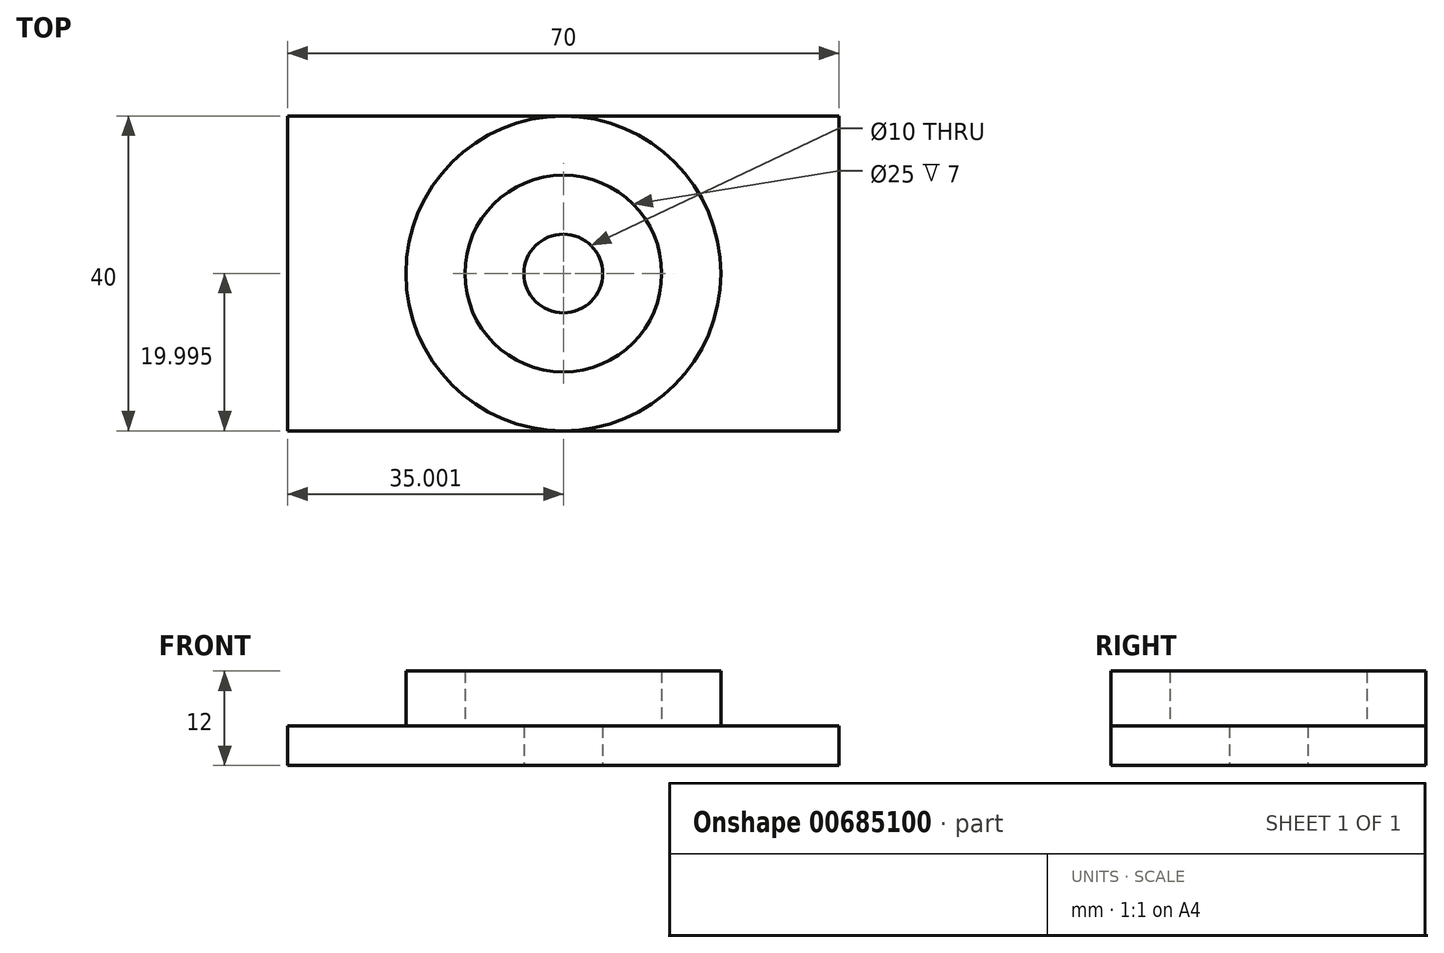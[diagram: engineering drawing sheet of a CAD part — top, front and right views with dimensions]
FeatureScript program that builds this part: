
annotation { "Feature Type Name" : "Feature", "Feature Type Description" : "" }
export const myFeature = defineFeature(function(context is Context, id is Id, definition is map)
    precondition{}
    {
        {
            var Q0;
            Q0=qCreatedBy(makeId("Top.planeOp"),FACE);
            var sketch = newSketch(context, id + "F0", { "sketchPlane" : qUnion([Q0])});
            skLineSegment(sketch, "E0.bottom", {"start": v(-34, 23.4) * mm, "end": v(46, 23.4) * mm});
            skLineSegment(sketch, "E0.top", {"start": v(-34, -16.6) * mm, "end": v(46, -16.6) * mm});
            skLineSegment(sketch, "E0.left", {"start": v(-34, 23.4) * mm, "end": v(-34, -16.6) * mm});
            skLineSegment(sketch, "E0.right", {"start": v(46, 23.4) * mm, "end": v(46, -16.6) * mm});
            skCircle(sketch, "E1", {"center": v(6, 3.4) * mm, "radius": 20 * mm});
            skCircle(sketch, "E2", {"center": v(6, 3.4) * mm, "radius": 12.5 * mm});
            skCircle(sketch, "E3", {"center": v(6, 3.4) * mm, "radius": 5 * mm});
            skLineSegment(sketch, "E4.bottom", {"start": v(46, 23.4) * mm, "end": v(41, 23.4) * mm});
            skLineSegment(sketch, "E4.top", {"start": v(46, -16.6) * mm, "end": v(41, -16.6) * mm});
            skLineSegment(sketch, "E4.right", {"start": v(41, 23.4) * mm, "end": v(41, -16.6) * mm});
            skLineSegment(sketch, "E5.bottom", {"start": v(-34, 23.4) * mm, "end": v(-29, 23.4) * mm});
            skLineSegment(sketch, "E5.top", {"start": v(-34, -16.6) * mm, "end": v(-29, -16.6) * mm});
            skLineSegment(sketch, "E5.right", {"start": v(-29, 23.4) * mm, "end": v(-29, -16.6) * mm});
            skSolve(sketch);
        }
        {
            var Q0;
            Q0=makeQuery(id+"F0.imprint","IMPRINT",FACE,{"disambiguationData":[TD([[makeQuery(id+"F0.imprint","IMPRINT",EDGE,{"derivedFrom":sQuery(id+"F0.wireOp",EDGE,"E2")}),1.0]])]});
            extrude(context, id + "F1", {"entities" : qUnion([Q0]), "depth" : 5 * mm, "offsetDistance" : 25 * mm});
        }
        {
            var Q0;
            Q0=makeQuery(id+"F0.imprint","IMPRINT",FACE,{"disambiguationData":[TD([[makeQuery(id+"F0.imprint","IMPRINT",EDGE,{"derivedFrom":sQuery(id+"F0.wireOp",EDGE,"E2")}),-1.0]])]});
            extrude(context, id + "F2", {"entities" : qUnion([Q0]), "operationType" : NewBodyOperationType.ADD, "depth" : 12 * mm, "offsetDistance" : 25 * mm});
        }
        {
            var Q0;
            {var subQ0=sQuery(id+"F0.wireOp",EDGE,"E4.right");Q0=makeQuery(id+"F0.imprint","IMPRINT",FACE,{"disambiguationData":[TD([[makeQuery(id+"F0.imprint","IMPRINT",EDGE,{"derivedFrom":subQ0}),-1.0]])]});}
            var Q1;
            {var subQ0=sQuery(id+"F0.wireOp",EDGE,"E5.right");Q1=makeQuery(id+"F0.imprint","IMPRINT",FACE,{"disambiguationData":[TD([[makeQuery(id+"F0.imprint","IMPRINT",EDGE,{"derivedFrom":subQ0}),1.0]])]});}
            extrude(context, id + "F3", {"entities" : qUnion([Q0, Q1]), "operationType" : NewBodyOperationType.ADD, "depth" : 5 * mm, "offsetDistance" : 25 * mm});
        }
    });
